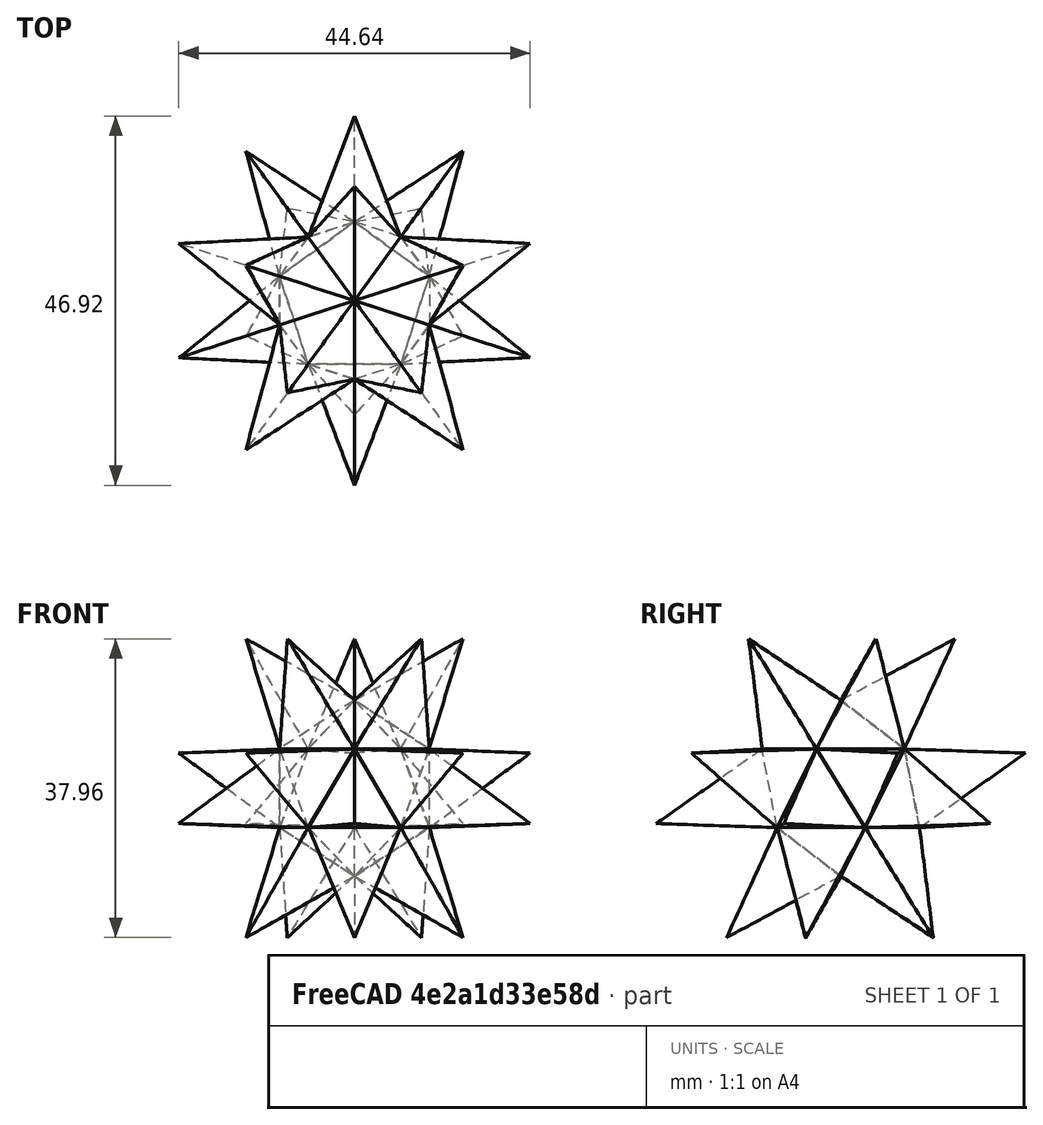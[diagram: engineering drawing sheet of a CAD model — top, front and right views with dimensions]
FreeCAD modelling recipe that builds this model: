
FCSTD DOCUMENT  (FreeCAD 0.18R13516 (Git))
Label: ESTRELA ICOSAEDRA
License: CreativeCommons Attribution-NonCommercial-ShareAlike
LicenseURL: http://creativecommons.org/licenses/by-nc-sa/4.0/
objects: Part::FeaturePython×5, Part::Compound×2, Part::RegularPolygon×1, Part::Vertex×1, Part::Loft×1
note: 10 computed .brp shape members not serialized (recipe doc carries the construction recipe); baked Part::Feature solids carry a one-line shape summary decoded from their .brp

FEATURE [Part::RegularPolygon] RegularPolygon  label="Regular polygon"
  AttacherType = Attacher::AttachEngine3D
  Circumradius = 6.77
  Polygon = 3
FEATURE [Part::Vertex] Vertex
  AttacherType = Attacher::AttachEngine3D
  X = 0
  Y = 0
  Z = 15
FEATURE [Part::Loft] Loft
  Closed = false
  MaxDegree = 5
  Placement = pos=(3.16229,-4.35241,12.0703) rot=(0.019574,-0.373526,0.927413;4.22577rad)
  Ruled = true
  Sections = -> [RegularPolygon,Vertex]
  Solid = true
FEATURE [Part::FeaturePython] ICOSAEDRO_01  # a2plus imported part (geometry in sourceFile) (typed FeaturePython)
  Placement = pos=(0,0,0) rot=(0,0,1;0.314159rad)
  fixedPosition = true
  sourceFile = <userpath>/WORK/FREECAD/70- ICOSAEDRO/ICOSAEDRO.FCStd
  timeLastImport = 1.53522e+09
  updateColors = true
FEATURE [Part::FeaturePython] Clone  label="Loft001"  # Draft clone (typed FeaturePython)
  AttacherType = Attacher::AttachEngine3D
  Fuse = false
  Objects = -> [Loft]
  Placement = pos=(5.13136,-7.06272,6.64981) rot=(-0.83404,-0.04371,-0.549969;4.54695rad)
  Scale = (1,1,1)
FEATURE [Part::FeaturePython] Clone001  label="Loft002"  # Draft clone (typed FeaturePython)
  AttacherType = Attacher::AttachEngine3D
  Fuse = false
  Objects = -> [Clone]
  Placement = pos=(0.0148605,-8.72517,3.32491) rot=(-0.610383,0.610383,-0.504842;4.07662rad)
  Scale = (1,1,1)
FEATURE [Part::FeaturePython] Clone002  label="Loft003"  # Draft clone (typed FeaturePython)
  AttacherType = Attacher::AttachEngine3D
  Fuse = false
  Objects = -> [Clone001]
  Placement = pos=(0.0148308,-5.40025,-2.0548) rot=(-0.687707,-0.687713,0.232616;3.59869rad)
  Scale = (1,1,1)
FEATURE [Part::Compound] Compound
  Links = -> [Loft,Clone,Clone001,Clone002]
FEATURE [Part::FeaturePython] Array  # Draft array (typed FeaturePython)
  Angle = 360
  ArrayType = 1
  Axis = (0,0,1)
  Base = -> Compound
  Center = (0,0,0)
  Fuse = false
  IntervalAxis = (0,0,0)
  IntervalX = (1,0,0)
  IntervalY = (0,1,0)
  IntervalZ = (0,0,0)
  NumberPolar = 5
  NumberX = 2
  NumberY = 2
  NumberZ = 1
FEATURE [Part::Compound] Compound001
  Links = -> [ICOSAEDRO_01,Array]
